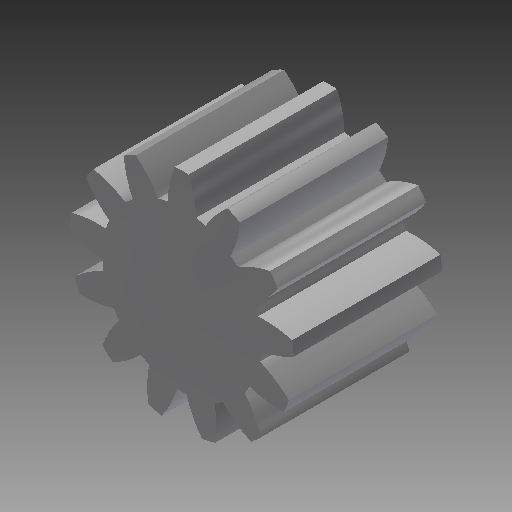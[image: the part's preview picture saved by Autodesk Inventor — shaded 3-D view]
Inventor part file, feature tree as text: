
AUTODESK INVENTOR PART (.ipt)
format: ipt  version: 2019 (Build 230136000, 136)  size: 207,360 bytes
history: native  units: mm (DEFAULTED — no unit token found)
features: plane x3, other x3, sketch x2, extrude x1
ambient origin geometry x8: Origin, YZ Plane, XZ Plane, XY Plane, X Axis, Y Axis, Z Axis, Center Point
bodies: Solid1 (feature_tree)
feature tree (9):
  extrude  "Extrusion1"  Depth=6.35mm TaperAngle=0.0deg
  plane  "Work Plane1"
  plane  "Work Plane2"
  plane  "Work Plane3"
  other  "Spur Gear"
  sketch  "Sketch1"  dims[d0=9.596692mm d1=6.35mm d2=0.0mm]
  sketch  "Sketch2"  dims[d3=8.388398mm d4=76.2mm d5=0.0mm d6=0.0mm d7=2.41661mm d9=0.0mm d14=0.0mm d15=37.74779mm d16=0.0mm d17=0.0mm d18=0.0mm d19=37.74779mm]
  other  "Srf1"
  other  "Pitch Diameter"
